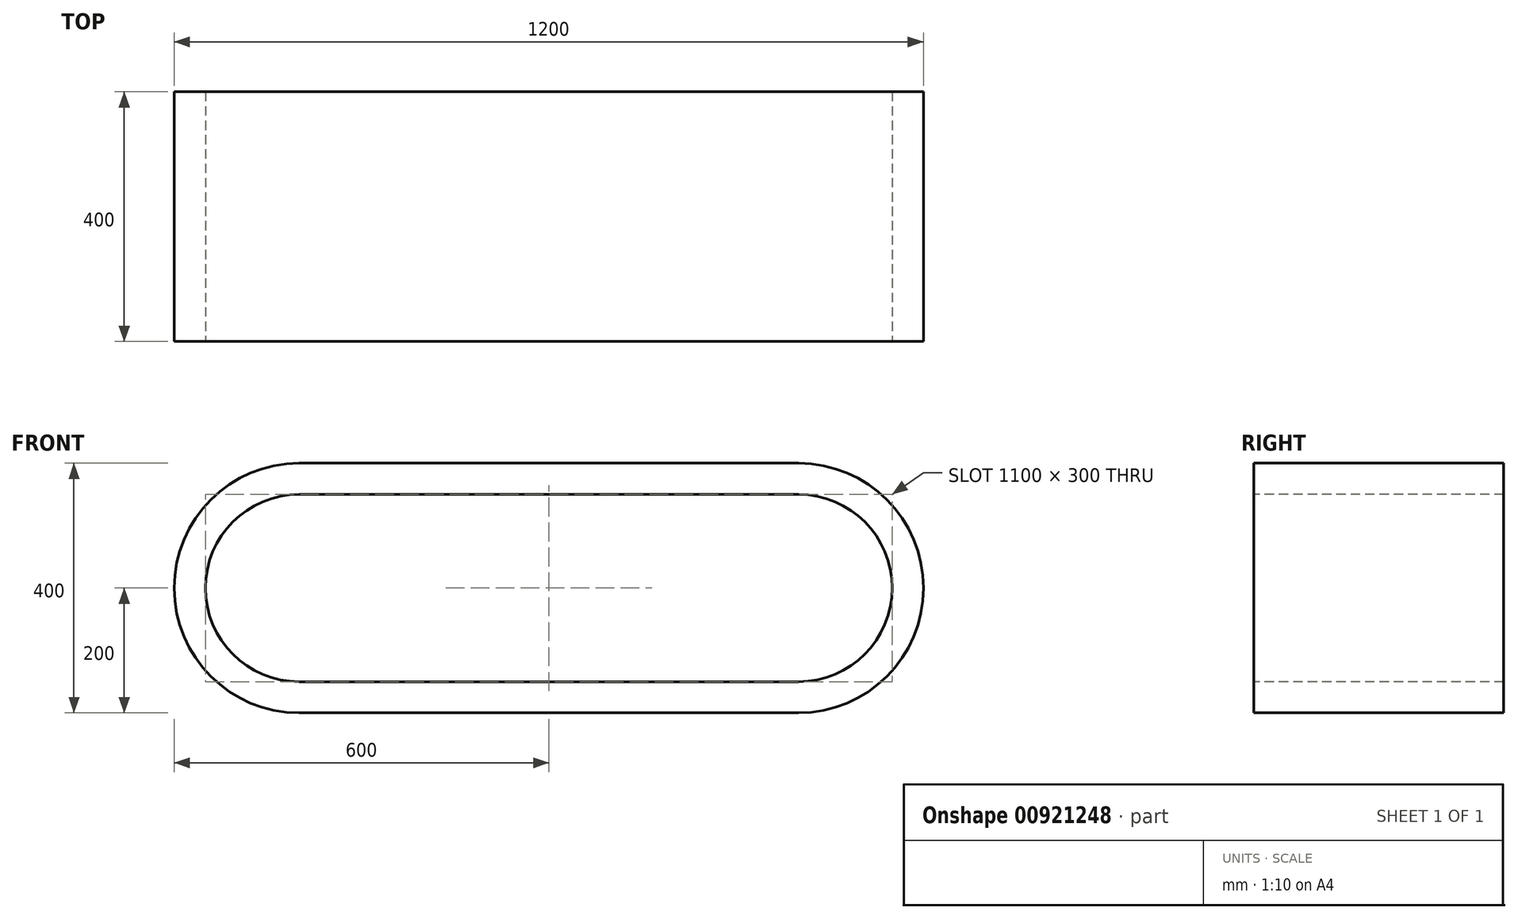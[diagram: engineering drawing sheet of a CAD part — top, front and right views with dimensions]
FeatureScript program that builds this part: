
annotation { "Feature Type Name" : "Feature", "Feature Type Description" : "" }
export const myFeature = defineFeature(function(context is Context, id is Id, definition is map)
    precondition{}
    {
        {
            var Q0;
            Q0=qCreatedBy(makeId("Front.planeOp"),FACE);
            var sketch = newSketch(context, id + "F0", { "sketchPlane" : qUnion([Q0])});
            skLineSegment(sketch, "E0.bottom", {"start": v(400, 200) * mm, "end": v(-400, 200) * mm});
            skLineSegment(sketch, "E0.top", {"start": v(400, -200) * mm, "end": v(-400, -200) * mm});
            skLineSegment(sketch, "E0.left", {"start": v(400, 200) * mm, "end": v(400, -200) * mm, "construction": true});
            skLineSegment(sketch, "E0.right", {"start": v(-400, 200) * mm, "end": v(-400, -200) * mm, "construction": true});
            skPoint(sketch, "E0.middle", {"position": v(0, 0) * mm});
            skArc(sketch, "E1", {"start": v(400, -200) * mm, "mid": v(600, 0) * mm, "end": v(400, 200) * mm});
            skArc(sketch, "E2", {"start": v(-400, 200) * mm, "mid": v(-600, 0) * mm, "end": v(-400, -200) * mm});
            skLineSegment(sketch, "E3", {"start": v(-600, 0) * mm, "end": v(600, 0) * mm, "construction": true});
            skSolve(sketch);
        }
        {
            var Q0;
            Q0=makeQuery(id+"F0.imprint","IMPRINT",FACE,{"disambiguationData":[TD([[makeQuery(id+"F0.imprint","IMPRINT",EDGE,{"derivedFrom":sQuery(id+"F0.wireOp",EDGE,"E0.bottom")}),1.0]])]});
            var sketch = newSketch(context, id + "F1", { "sketchPlane" : qUnion([Q0])});
            skSolve(sketch);
        }
        {
            var Q0;
            Q0=makeQuery(id+"F1.imprint","IMPRINT",FACE,{"disambiguationData":[TD([[makeQuery(id+"F1.imprint","IMPRINT",EDGE,{"derivedFrom":makeQuery(id+"F0.imprint","IMPRINT",EDGE,{"derivedFrom":sQuery(id+"F0.wireOp",EDGE,"E0.bottom")})}),1.0]])]});
            extrude(context, id + "F2", {"entities" : qUnion([Q0]), "oppositeDirection" : true, "depth" : 200 * mm, "offsetDistance" : 25 * mm, "hasSecondDirection" : true, "secondDirectionOppositeDirection" : false, "secondDirectionDepth" : 200 * mm});
        }
        {
            var Q0;
            Q0=makeQuery(id+"F2.opExtrude","CAP_FACE",FACE,{"disambiguationData":[OSD([sQuery(id+"F0.wireOp",EDGE,"E0.bottom"),sQuery(id+"F0.wireOp",EDGE,"E0.top"),sQuery(id+"F0.wireOp",EDGE,"E1"),sQuery(id+"F0.wireOp",EDGE,"E2")])],"isStart":true});
            var sketch = newSketch(context, id + "F3", { "sketchPlane" : qUnion([Q0])});
            skLineSegment(sketch, "E4.bottom", {"start": v(400, -150) * mm, "end": v(-400, -150) * mm});
            skLineSegment(sketch, "E4.top", {"start": v(400, 150) * mm, "end": v(-400, 150) * mm});
            skLineSegment(sketch, "E4.left", {"start": v(400, -150) * mm, "end": v(400, 150) * mm, "construction": true});
            skLineSegment(sketch, "E4.right", {"start": v(-400, -150) * mm, "end": v(-400, 150) * mm, "construction": true});
            skPoint(sketch, "E4.middle", {"position": v(0, 0) * mm});
            skArc(sketch, "E5", {"start": v(-400, 150) * mm, "mid": v(-550, 0) * mm, "end": v(-400, -150) * mm});
            skArc(sketch, "E6", {"start": v(400, -150) * mm, "mid": v(550, 0) * mm, "end": v(400, 150) * mm});
            skSolve(sketch);
        }
        {
            var Q0;
            Q0 = qSketchRegion(id + "F3", true);
            extrude(context, id + "F4", {"entities" : qUnion([Q0]), "operationType" : NewBodyOperationType.REMOVE, "oppositeDirection" : true, "depth" : 4000 * mm, "offsetDistance" : 25 * mm});
        }
    });
